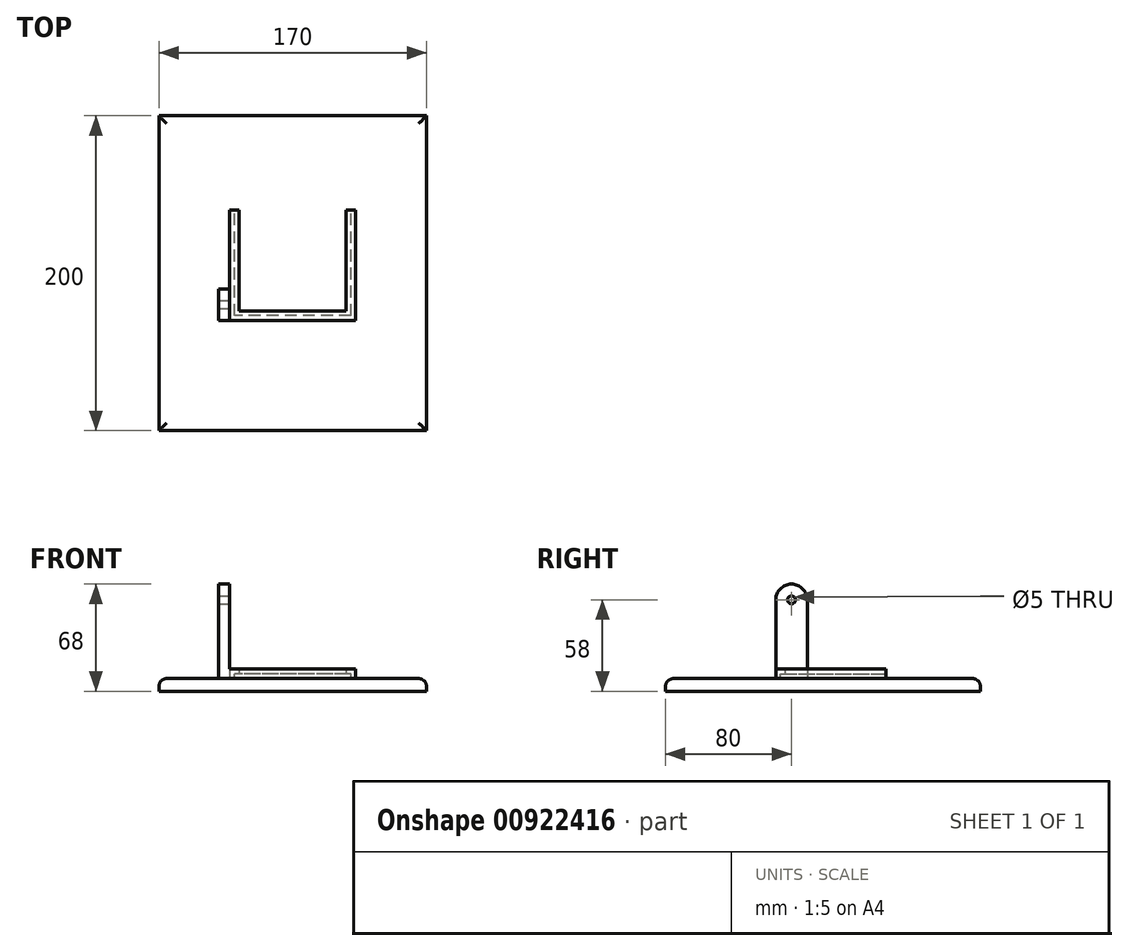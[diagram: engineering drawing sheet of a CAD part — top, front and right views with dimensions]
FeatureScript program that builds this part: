
annotation { "Feature Type Name" : "Feature", "Feature Type Description" : "" }
export const myFeature = defineFeature(function(context is Context, id is Id, definition is map)
    precondition{}
    {
        {
            var Q0;
            Q0=qCreatedBy(makeId("Top.planeOp"),FACE);
            var sketch = newSketch(context, id + "F0", { "sketchPlane" : qUnion([Q0])});
            skLineSegment(sketch, "E0.bottom", {"start": v(-85, 100) * mm, "end": v(85, 100) * mm});
            skLineSegment(sketch, "E0.top", {"start": v(-85, -100) * mm, "end": v(85, -100) * mm});
            skLineSegment(sketch, "E0.left", {"start": v(-85, 100) * mm, "end": v(-85, -100) * mm});
            skLineSegment(sketch, "E0.right", {"start": v(85, 100) * mm, "end": v(85, -100) * mm});
            skSolve(sketch);
        }
        {
            var Q0;
            Q0=makeQuery(id+"F0.imprint","IMPRINT",FACE,{"disambiguationData":[TD([[makeQuery(id+"F0.imprint","IMPRINT",EDGE,{"derivedFrom":sQuery(id+"F0.wireOp",EDGE,"E0.bottom")}),-1.0]])]});
            extrude(context, id + "F1", {"entities" : qUnion([Q0]), "depth" : 8 * mm, "offsetDistance" : 25 * mm});
        }
        {
            var Q0;
            Q0=makeQuery(id+"F1.opExtrude","CAP_EDGE",EDGE,{"disambiguationData":[OSD([sQuery(id+"F0.wireOp",EDGE,"E0.top")])],"isStart":false});
            var Q1;
            Q1=makeQuery(id+"F1.opExtrude","CAP_EDGE",EDGE,{"disambiguationData":[OSD([sQuery(id+"F0.wireOp",EDGE,"E0.left")])],"isStart":false});
            var Q2;
            Q2=makeQuery(id+"F1.opExtrude","CAP_EDGE",EDGE,{"disambiguationData":[OSD([sQuery(id+"F0.wireOp",EDGE,"E0.right")])],"isStart":false});
            var Q3;
            Q3=makeQuery(id+"F1.opExtrude","CAP_EDGE",EDGE,{"disambiguationData":[OSD([sQuery(id+"F0.wireOp",EDGE,"E0.bottom")])],"isStart":false});
            fillet(context, id + "F2", {"entities" : qUnion([Q0, Q1, Q2, Q3]), "radius" : 5 * mm, "tangentPropagation" : true, "allowEdgeOverflow" : false});
        }
        {
            var Q0;
            Q0=makeQuery(id+"F1.opExtrude","CAP_FACE",FACE,{"disambiguationData":[OSD([sQuery(id+"F0.wireOp",EDGE,"E0.bottom"),sQuery(id+"F0.wireOp",EDGE,"E0.top"),sQuery(id+"F0.wireOp",EDGE,"E0.left"),sQuery(id+"F0.wireOp",EDGE,"E0.right")])],"isStart":false});
            var sketch = newSketch(context, id + "F3", { "sketchPlane" : qUnion([Q0])});
            skLineSegment(sketch, "E1.bottom", {"start": v(-47, -10) * mm, "end": v(-40, -10) * mm});
            skLineSegment(sketch, "E1.top", {"start": v(-47, -30) * mm, "end": v(-40, -30) * mm});
            skLineSegment(sketch, "E1.left", {"start": v(-47, -10) * mm, "end": v(-47, -30) * mm});
            skLineSegment(sketch, "E1.right", {"start": v(-40, -10) * mm, "end": v(-40, -30) * mm});
            skSolve(sketch);
        }
        {
            var Q0;
            Q0=makeQuery(id+"F3.imprint","IMPRINT",FACE,{"disambiguationData":[TD([[makeQuery(id+"F3.imprint","IMPRINT",EDGE,{"derivedFrom":sQuery(id+"F3.wireOp",EDGE,"E1.bottom")}),-1.0]])]});
            extrude(context, id + "F4", {"entities" : qUnion([Q0]), "operationType" : NewBodyOperationType.ADD, "depth" : 60 * mm, "offsetDistance" : 25 * mm});
        }
        {
            var Q0;
            Q0=makeQuery(id+"F4.opExtrude","CAP_EDGE",EDGE,{"disambiguationData":[OSD([sQuery(id+"F3.wireOp",EDGE,"E1.top")])],"isStart":false});
            var Q1;
            Q1=makeQuery(id+"F4.opExtrude","CAP_EDGE",EDGE,{"disambiguationData":[OSD([sQuery(id+"F3.wireOp",EDGE,"E1.bottom")])],"isStart":false});
            fillet(context, id + "F5", {"entities" : qUnion([Q0, Q1]), "radius" : 10 * mm, "tangentPropagation" : true, "allowEdgeOverflow" : false});
        }
        {
            var Q0;
            Q0=makeQuery(id+"F4.opExtrude","SWEPT_FACE",FACE,{"disambiguationData":[OSD([sQuery(id+"F3.wireOp",EDGE,"E1.right")])]});
            var sketch = newSketch(context, id + "F6", { "sketchPlane" : qUnion([Q0])});
            skCircle(sketch, "E2", {"center": v(-20, 58) * mm, "radius": 2.5 * mm});
            skSolve(sketch);
        }
        {
            var Q0;
            Q0=makeQuery(id+"F6.imprint","IMPRINT",FACE,{"disambiguationData":[TD([[makeQuery(id+"F6.imprint","IMPRINT",EDGE,{"derivedFrom":sQuery(id+"F6.wireOp",EDGE,"E2")}),1.0]])]});
            extrude(context, id + "F7", {"entities" : qUnion([Q0]), "operationType" : NewBodyOperationType.REMOVE, "endBound" : BoundingType.THROUGH_ALL, "oppositeDirection" : true, "depth" : 25 * mm, "offsetDistance" : 25 * mm});
        }
        {
            var Q0;
            Q0=makeQuery(id+"F1.opExtrude","CAP_FACE",FACE,{"disambiguationData":[OSD([sQuery(id+"F0.wireOp",EDGE,"E0.bottom"),sQuery(id+"F0.wireOp",EDGE,"E0.top"),sQuery(id+"F0.wireOp",EDGE,"E0.left"),sQuery(id+"F0.wireOp",EDGE,"E0.right")])],"isStart":false});
            var sketch = newSketch(context, id + "F8", { "sketchPlane" : qUnion([Q0])});
            skLineSegment(sketch, "E3.bottom", {"start": v(-40, -30) * mm, "end": v(40, -30) * mm});
            skLineSegment(sketch, "E3.top", {"start": v(-40, 40) * mm, "end": v(40, 40) * mm});
            skLineSegment(sketch, "E3.left", {"start": v(-40, -30) * mm, "end": v(-40, 40) * mm});
            skLineSegment(sketch, "E3.right", {"start": v(40, -30) * mm, "end": v(40, 40) * mm});
            skSolve(sketch);
        }
        {
            var Q0;
            Q0=makeQuery(id+"F8.imprint","IMPRINT",FACE,{"disambiguationData":[TD([[makeQuery(id+"F8.imprint","IMPRINT",EDGE,{"derivedFrom":sQuery(id+"F8.wireOp",EDGE,"E3.bottom")}),1.0]])]});
            extrude(context, id + "F9", {"entities" : qUnion([Q0]), "operationType" : NewBodyOperationType.ADD, "depth" : 6 * mm, "offsetDistance" : 25 * mm});
        }
        {
            var Q0;
            Q0=makeQuery(id+"F9.opExtrude","SWEPT_FACE",FACE,{"disambiguationData":[OSD([sQuery(id+"F8.wireOp",EDGE,"E3.top")])]});
            var sketch = newSketch(context, id + "F10", { "sketchPlane" : qUnion([Q0])});
            skLineSegment(sketch, "E4.bottom", {"start": v(-37, 11) * mm, "end": v(37, 11) * mm});
            skLineSegment(sketch, "E4.top", {"start": v(-37, 8) * mm, "end": v(37, 8) * mm});
            skLineSegment(sketch, "E4.left", {"start": v(-37, 8) * mm, "end": v(-37, 11) * mm});
            skLineSegment(sketch, "E4.right", {"start": v(37, 8) * mm, "end": v(37, 11) * mm});
            skSolve(sketch);
        }
        {
            var Q0;
            Q0=makeQuery(id+"F10.imprint","IMPRINT",FACE,{"disambiguationData":[TD([[makeQuery(id+"F10.imprint","IMPRINT",EDGE,{"derivedFrom":sQuery(id+"F10.wireOp",EDGE,"E4.bottom")}),-1.0]])]});
            extrude(context, id + "F11", {"entities" : qUnion([Q0]), "operationType" : NewBodyOperationType.REMOVE, "oppositeDirection" : true, "depth" : 67 * mm, "offsetDistance" : 25 * mm});
        }
        {
            var Q0;
            Q0=makeQuery(id+"F9.opExtrude","SWEPT_FACE",FACE,{"disambiguationData":[OSD([sQuery(id+"F8.wireOp",EDGE,"E3.top")])]});
            var sketch = newSketch(context, id + "F12", { "sketchPlane" : qUnion([Q0])});
            skLineSegment(sketch, "E5.bottom", {"start": v(-34, 11) * mm, "end": v(34, 11) * mm});
            skLineSegment(sketch, "E5.top", {"start": v(-34, 14) * mm, "end": v(34, 14) * mm});
            skLineSegment(sketch, "E5.left", {"start": v(-34, 14) * mm, "end": v(-34, 11) * mm});
            skLineSegment(sketch, "E5.right", {"start": v(34, 14) * mm, "end": v(34, 11) * mm});
            skSolve(sketch);
        }
        {
            var Q0;
            Q0=makeQuery(id+"F12.imprint","IMPRINT",FACE,{"disambiguationData":[TD([[makeQuery(id+"F12.imprint","IMPRINT",EDGE,{"derivedFrom":sQuery(id+"F12.wireOp",EDGE,"E5.bottom")}),1.0]])]});
            extrude(context, id + "F13", {"entities" : qUnion([Q0]), "operationType" : NewBodyOperationType.REMOVE, "oppositeDirection" : true, "depth" : 64 * mm, "offsetDistance" : 25 * mm});
        }
    });
